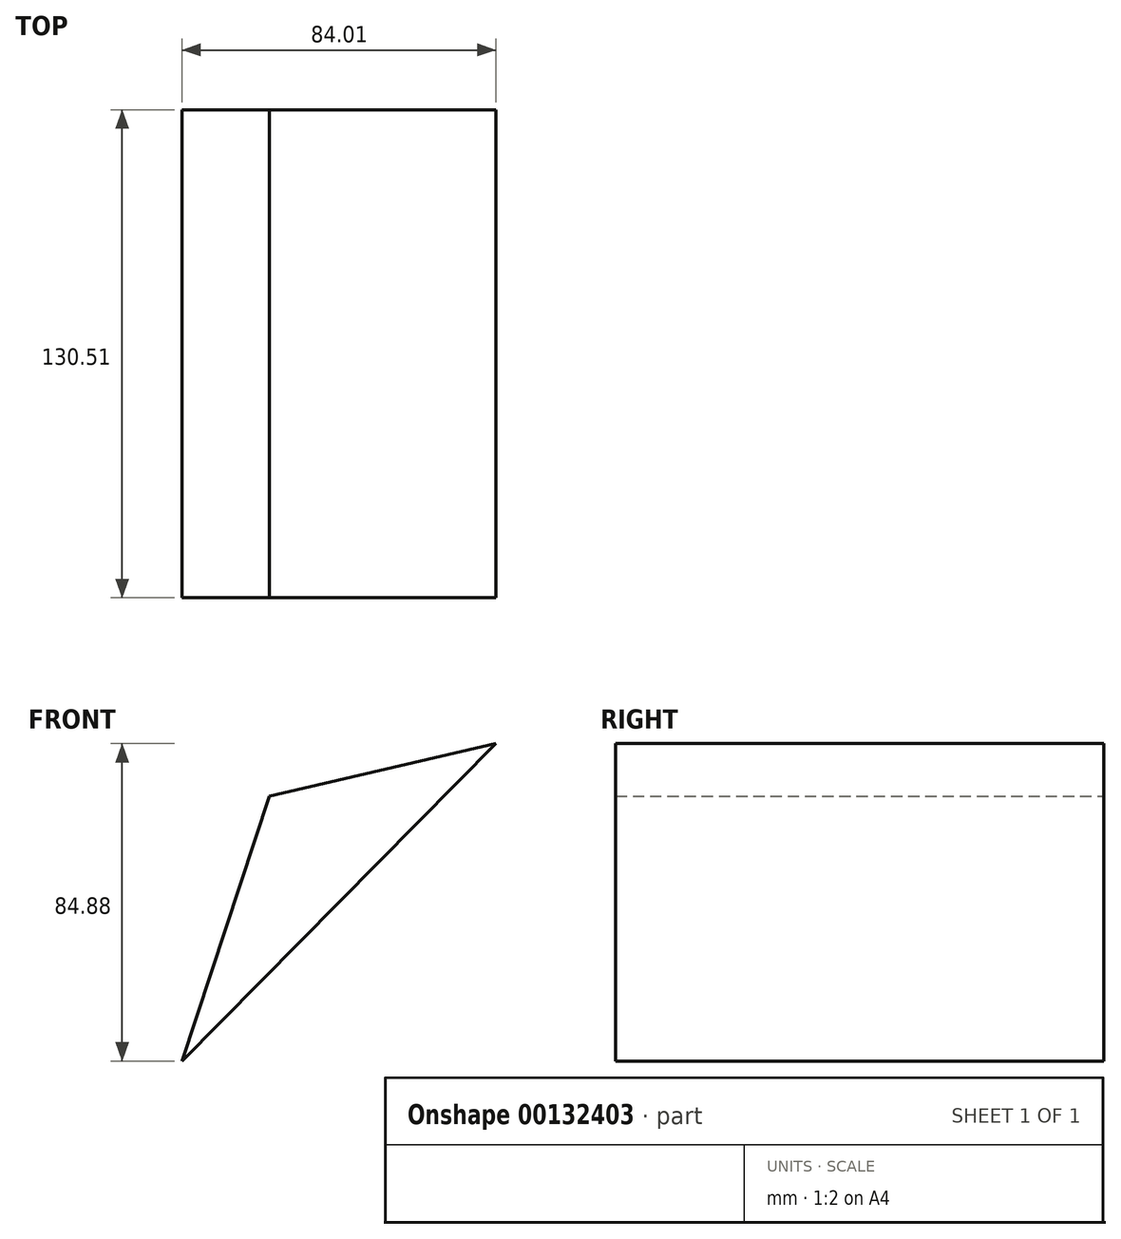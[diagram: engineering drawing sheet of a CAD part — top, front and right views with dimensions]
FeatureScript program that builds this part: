
annotation { "Feature Type Name" : "Feature", "Feature Type Description" : "" }
export const myFeature = defineFeature(function(context is Context, id is Id, definition is map)
    precondition{}
    {
        {
            var Q0;
            Q0=qCreatedBy(makeId("Front.planeOp"),FACE);
            var sketch = newSketch(context, id + "F0", { "sketchPlane" : qUnion([Q0])});
            skLineSegment(sketch, "E0", {"start": v(-97, 56.22) * mm, "end": v(-120.38, -14.62) * mm});
            skLineSegment(sketch, "E1", {"start": v(-120.38, -14.62) * mm, "end": v(-36.37, 70.26) * mm});
            skLineSegment(sketch, "E2", {"start": v(-36.37, 70.26) * mm, "end": v(-97, 56.22) * mm});
            skSolve(sketch);
        }
        {
            var Q0;
            Q0 = qSketchRegion(id + "F0", true);
            extrude(context, id + "F1", {"entities" : qUnion([Q0]), "depth" : 130.5 * mm});
        }
    });
